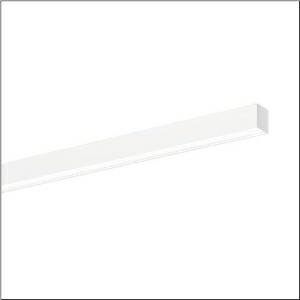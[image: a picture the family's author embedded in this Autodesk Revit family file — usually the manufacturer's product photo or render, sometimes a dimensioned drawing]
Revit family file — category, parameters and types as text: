
# Revit family: silica_r__21_51mx20tct5w_c7ea
name_source: partatom
category: Lighting Fixtures
units: mm (PartAtom-declared; Revit-internal decimal feet)

## family parameters
Cut with Voids When Loaded = No
Host = Face
Light Source = No
Part Type = Normal
Room Calculation Point = No
Round Connector Dimension = Use Diameter
Shared = No

## types (1)
- --- (1 x LED, 6000 lm, 51.3 W, 6500K)
    Apparent Load = 51 VA
    CIE Flux Codes = 48 79 96 100 100
    Color Rendering = 80
    Color Temperature = 6500K
    Default Elevation = 1800 mm
    Description = Silica® 21, office luminaire, primary optical cover: cover, of PMMA, opal, light emission: direct distribution, primary light characteristic: symmetric, installation type: surface-mounted, LED, rated luminous flux: 6.000lm, luminous efficacy: 112lm/W, light colour: 8tw, colour temperature: 2700..6500K, control gear: DALI DT8, with terminal, 3+2-pole, max. 2.5mm², mains connection: 220..240V, AC, 50/60Hz, rated input power: 53.8W, luminaire housing, of aluminium, traffic white (RAL 9016), length: 3.004mm, width: 53mm, height: 53mm, protection rating (complete): IP20, insulation class (complete): insulation class I (protective earthing), certification: CE, permissible operating ambient temperature: 0..+35°C, standard: EN 50419, packaging unit: 1 piece
    Height = 53 mm
    Lamp = 1 x LED
    Lamp Light Flux = 6000 lm
    Lamp Power = 51.3 W
    Lamp count = 1
    Length = 3004 mm
    Luminous efficacy = 117 lm/W
    Manufacturer = Siteco
    ModVariant = No
    Model = 51MX20TCT5W
    Mounting Place = Ceiling
    Mounting Type = Surface mounted
    Number of Poles = 1
    OnlyDefault = Yes
    Power Factor = 1
    Product Name = Silica® 21
    Product group = office luminaire | ceiling mounted
    ProductGroupID = 302
    Protection Class = Protection class I
    Protection Degree = IP 20
    RLX_Detail_Level = 1
    RLX_Emergency_Light_Flux = 0 lm
    RLX_Emergency_Type = 0
    RLX_Emergency_Type_DB = No
    RlxData = <blob elided: 20561 chars, md5=d682fa0e>
    Socket = socket
    Standby Power = 0 W
    System Light Flux = 6000 lm
    System Power = 51 W
    Type Comments = individual setting
    Type Image = l_1335877.jpg
    URL = http://relux.com
    VarID = @adj_139698
    Voltage = 0 V
    Weight = 0.00 kg
    Width = 53 mm

## geometry (parser evidence)
native form markers: Blend x4, Sweep x11
no freeform markers — native parametric forms only
